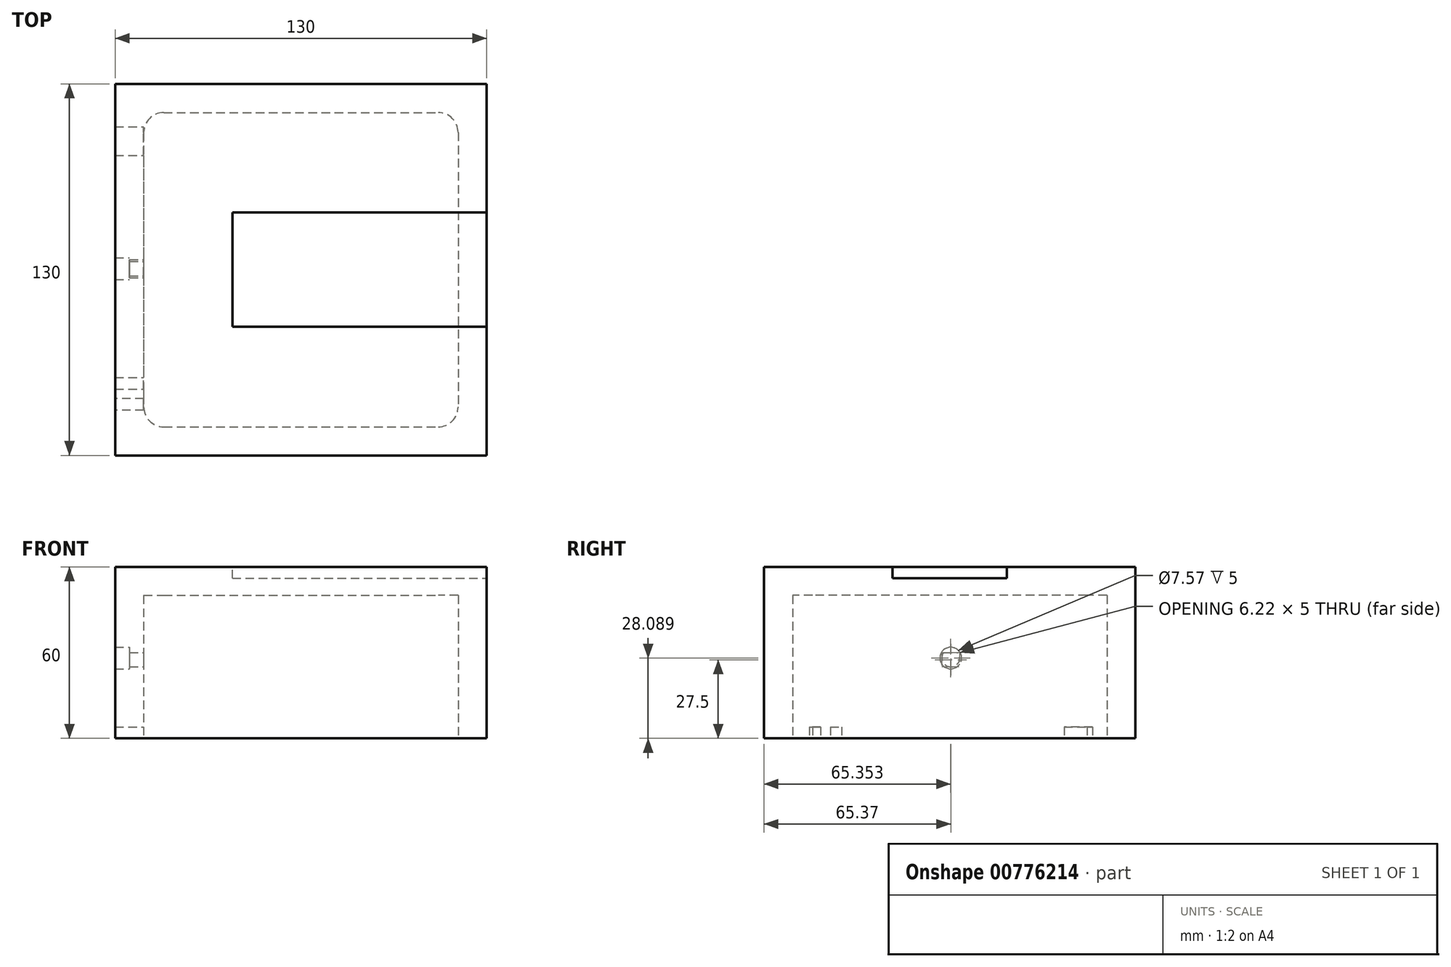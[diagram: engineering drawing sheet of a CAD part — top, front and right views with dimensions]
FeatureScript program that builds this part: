
annotation { "Feature Type Name" : "Feature", "Feature Type Description" : "" }
export const myFeature = defineFeature(function(context is Context, id is Id, definition is map)
    precondition{}
    {
        {
            var Q0;
            Q0=qCreatedBy(makeId("Top.planeOp"),FACE);
            var sketch = newSketch(context, id + "F0", { "sketchPlane" : qUnion([Q0])});
            skLineSegment(sketch, "E0.bottom", {"start": v(-65, 65) * mm, "end": v(65, 65) * mm});
            skLineSegment(sketch, "E0.top", {"start": v(-65, -65) * mm, "end": v(65, -65) * mm});
            skLineSegment(sketch, "E0.left", {"start": v(-65, 65) * mm, "end": v(-65, -65) * mm});
            skLineSegment(sketch, "E0.right", {"start": v(65, 65) * mm, "end": v(65, -65) * mm});
            skPoint(sketch, "E0.middle", {"position": v(0, 0) * mm});
            skSolve(sketch);
        }
        {
            var Q0;
            Q0=qSketchRegion(id+"F0",true);
            extrude(context, id + "F1", {"entities" : qUnion([Q0]), "depth" : 60 * mm, "offsetDistance" : 25 * mm});
        }
        {
            var Q0;
            Q0=qCreatedBy(makeId("Top.planeOp"),FACE);
            var sketch = newSketch(context, id + "F2", { "sketchPlane" : qUnion([Q0])});
            skLineSegment(sketch, "E1.bottom", {"start": v(-55, 55) * mm, "end": v(55, 55) * mm});
            skLineSegment(sketch, "E1.top", {"start": v(-55, -55) * mm, "end": v(55, -55) * mm});
            skLineSegment(sketch, "E1.left", {"start": v(-55, 55) * mm, "end": v(-55, -55) * mm});
            skLineSegment(sketch, "E1.right", {"start": v(55, 55) * mm, "end": v(55, -55) * mm});
            skPoint(sketch, "E1.middle", {"position": v(0, 0) * mm});
            skSolve(sketch);
        }
        {
            var Q0;
            Q0=makeQuery(id+"F2.imprint","IMPRINT",FACE,{"disambiguationData":[TD([[makeQuery(id+"F2.imprint","IMPRINT",EDGE,{"derivedFrom":sQuery(id+"F2.wireOp",EDGE,"E1.bottom")}),-1.0]])]});
            extrude(context, id + "F3", {"entities" : qUnion([Q0]), "operationType" : NewBodyOperationType.REMOVE, "depth" : 50 * mm, "offsetDistance" : 25 * mm});
        }
        {
            var Q0;
            Q0=makeQuery(id+"F1.opExtrude","CAP_FACE",FACE,{"disambiguationData":[OSD([sQuery(id+"F0.wireOp",EDGE,"E0.bottom"),sQuery(id+"F0.wireOp",EDGE,"E0.top"),sQuery(id+"F0.wireOp",EDGE,"E0.left"),sQuery(id+"F0.wireOp",EDGE,"E0.right")])],"isStart":false});
            var sketch = newSketch(context, id + "F4", { "sketchPlane" : qUnion([Q0])});
            skLineSegment(sketch, "E2.bottom", {"start": v(-24, -20) * mm, "end": v(65, -20) * mm});
            skLineSegment(sketch, "E2.top", {"start": v(-24, 20) * mm, "end": v(65, 20) * mm});
            skLineSegment(sketch, "E2.left", {"start": v(-24, -20) * mm, "end": v(-24, 20) * mm});
            skLineSegment(sketch, "E2.right", {"start": v(65, -20) * mm, "end": v(65, 20) * mm});
            skSolve(sketch);
        }
        {
            var Q0;
            Q0=qSketchRegion(id+"F4",true);
            extrude(context, id + "F5", {"entities" : qUnion([Q0]), "operationType" : NewBodyOperationType.REMOVE, "oppositeDirection" : true, "depth" : 4 * mm, "offsetDistance" : 25 * mm});
        }
        {
            var Q0;
            Q0=makeQuery(id+"F3.boolean.opBoolean","COPY",EDGE,{"derivedFrom":makeQuery(id+"F3.opExtrude","SWEPT_EDGE",EDGE,{"disambiguationData":[OSD([sQuery(id+"F2.wireOp",EDGE,"E1.top"),sQuery(id+"F2.wireOp",EDGE,"E1.right")])]})});
            var Q1;
            Q1=makeQuery(id+"F3.boolean.opBoolean","COPY",EDGE,{"derivedFrom":makeQuery(id+"F3.opExtrude","SWEPT_EDGE",EDGE,{"disambiguationData":[OSD([sQuery(id+"F2.wireOp",EDGE,"E1.bottom"),sQuery(id+"F2.wireOp",EDGE,"E1.right")])]})});
            var Q2;
            Q2=makeQuery(id+"F3.boolean.opBoolean","COPY",EDGE,{"derivedFrom":makeQuery(id+"F3.opExtrude","SWEPT_EDGE",EDGE,{"disambiguationData":[OSD([sQuery(id+"F2.wireOp",EDGE,"E1.bottom"),sQuery(id+"F2.wireOp",EDGE,"E1.left")])]})});
            var Q3;
            Q3=makeQuery(id+"F3.boolean.opBoolean","COPY",EDGE,{"derivedFrom":makeQuery(id+"F3.opExtrude","SWEPT_EDGE",EDGE,{"disambiguationData":[OSD([sQuery(id+"F2.wireOp",EDGE,"E1.top"),sQuery(id+"F2.wireOp",EDGE,"E1.left")])]})});
            fillet(context, id + "F6", {"entities" : qUnion([Q0, Q1, Q2, Q3]), "radius" : 7 * mm, "tangentPropagation" : true, "allowEdgeOverflow" : false});
        }
        {
            var Q0;
            Q0=makeQuery(id+"F0.imprint","IMPRINT",FACE,{"disambiguationData":[TD([[makeQuery(id+"F0.imprint","IMPRINT",EDGE,{"derivedFrom":sQuery(id+"F0.wireOp",EDGE,"E0.bottom")}),-1.0]])]});
            var sketch = newSketch(context, id + "F7", { "sketchPlane" : qUnion([Q0])});
            skLineSegment(sketch, "E3.bottom", {"start": v(-65, -41.78) * mm, "end": v(-55, -41.78) * mm});
            skLineSegment(sketch, "E3.top", {"start": v(-65, -37.78) * mm, "end": v(-55, -37.78) * mm});
            skLineSegment(sketch, "E3.left", {"start": v(-65, -41.78) * mm, "end": v(-65, -37.78) * mm});
            skLineSegment(sketch, "E3.right", {"start": v(-55, -41.78) * mm, "end": v(-55, -37.78) * mm});
            skPoint(sketch, "E3.middle", {"position": v(-60, -39.78) * mm});
            skSolve(sketch);
        }
        {
            var Q0;
            Q0=qSketchRegion(id+"F7",true);
            extrude(context, id + "F8", {"entities" : qUnion([Q0]), "operationType" : NewBodyOperationType.REMOVE, "depth" : 4 * mm, "offsetDistance" : 25 * mm});
        }
        {
            var Q0;
            Q0=makeQuery(id+"F0.imprint","IMPRINT",FACE,{"disambiguationData":[TD([[makeQuery(id+"F0.imprint","IMPRINT",EDGE,{"derivedFrom":sQuery(id+"F0.wireOp",EDGE,"E0.bottom")}),-1.0]])]});
            var sketch = newSketch(context, id + "F9", { "sketchPlane" : qUnion([Q0])});
            skLineSegment(sketch, "E4.bottom", {"start": v(-55, -49.14) * mm, "end": v(-65, -49.14) * mm});
            skLineSegment(sketch, "E4.top", {"start": v(-55, -45.14) * mm, "end": v(-65, -45.14) * mm});
            skLineSegment(sketch, "E4.left", {"start": v(-55, -49.14) * mm, "end": v(-55, -45.14) * mm});
            skLineSegment(sketch, "E4.right", {"start": v(-65, -49.14) * mm, "end": v(-65, -45.14) * mm});
            skSolve(sketch);
        }
        {
            var Q0;
            Q0=qSketchRegion(id+"F9",true);
            extrude(context, id + "F10", {"entities" : qUnion([Q0]), "operationType" : NewBodyOperationType.REMOVE, "depth" : 4 * mm, "offsetDistance" : 25 * mm});
        }
        {
            var Q0;
            Q0=makeQuery(id+"F0.imprint","IMPRINT",FACE,{"disambiguationData":[TD([[makeQuery(id+"F0.imprint","IMPRINT",EDGE,{"derivedFrom":sQuery(id+"F0.wireOp",EDGE,"E0.bottom")}),-1.0]])]});
            var sketch = newSketch(context, id + "F11", { "sketchPlane" : qUnion([Q0])});
            skLineSegment(sketch, "E5.bottom", {"start": v(-65, 50) * mm, "end": v(-55, 50) * mm});
            skLineSegment(sketch, "E5.top", {"start": v(-65, 40) * mm, "end": v(-55, 40) * mm});
            skLineSegment(sketch, "E5.left", {"start": v(-65, 40) * mm, "end": v(-65, 50) * mm});
            skLineSegment(sketch, "E5.right", {"start": v(-55, 40) * mm, "end": v(-55, 50) * mm});
            skSolve(sketch);
        }
        {
            var Q0;
            Q0=qSketchRegion(id+"F11",true);
            extrude(context, id + "F12", {"entities" : qUnion([Q0]), "operationType" : NewBodyOperationType.REMOVE, "depth" : 4 * mm, "offsetDistance" : 25 * mm});
        }
        {
            var Q0;
            Q0=makeQuery(id+"F1.opExtrude","SWEPT_FACE",FACE,{"disambiguationData":[OSD([sQuery(id+"F0.wireOp",EDGE,"E0.left")])]});
            cPlane(context, id + "F13", {"entities" : qUnion([Q0]), "cplaneType" : CPlaneType.OFFSET, "offset" : 10 * mm, "oppositeDirection" : true, "width" : 150 * mm, "height" : 150 * mm});
        }
        {
            var Q0;
            Q0=qCreatedBy(id+"F13.planeOp",FACE);
            var sketch = newSketch(context, id + "F14", { "sketchPlane" : qUnion([Q0])});
            skLineSegment(sketch, "E6", {"start": v(2.13, 30) * mm, "end": v(-2.87, 30) * mm});
            skArc(sketch, "E7", {"start": v(-2.87, 30) * mm, "mid": v(-0.37, 25) * mm, "end": v(2.13, 30) * mm});
            skSolve(sketch);
        }
        {
            var Q0;
            Q0 = qSketchRegion(id + "F14", true);
            extrude(context, id + "F15", {"entities" : qUnion([Q0]), "operationType" : NewBodyOperationType.REMOVE, "depth" : 5 * mm, "offsetDistance" : 25 * mm});
        }
        {
            var Q0;
            Q0=makeQuery(id+"F1.opExtrude","SWEPT_FACE",FACE,{"disambiguationData":[OSD([sQuery(id+"F0.wireOp",EDGE,"E0.left")])]});
            cPlane(context, id + "F16", {"entities" : qUnion([Q0]), "cplaneType" : CPlaneType.OFFSET, "offset" : 5 * mm, "oppositeDirection" : true, "width" : 150 * mm, "height" : 150 * mm});
        }
        {
            var Q0;
            Q0=qCreatedBy(id+"F16.planeOp",FACE);
            var sketch = newSketch(context, id + "F17", { "sketchPlane" : qUnion([Q0])});
            skCircle(sketch, "E8", {"center": v(-0.35, 28.09) * mm, "radius": 3.78 * mm});
            skPoint(sketch, "E8.first.point", {"position": v(-4.13, 27.87) * mm});
            skPoint(sketch, "E8.second.point", {"position": v(3.43, 27.95) * mm});
            skPoint(sketch, "E8.third.point", {"position": v(0, 31.86) * mm});
            skSolve(sketch);
        }
        {
            var Q0;
            Q0 = qSketchRegion(id + "F17", true);
            extrude(context, id + "F18", {"entities" : qUnion([Q0]), "operationType" : NewBodyOperationType.REMOVE, "depth" : 10 * mm, "offsetDistance" : 25 * mm});
        }
    });
